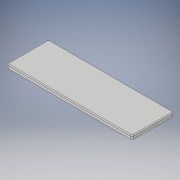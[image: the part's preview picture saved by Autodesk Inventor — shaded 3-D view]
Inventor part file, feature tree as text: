
AUTODESK INVENTOR PART (.ipt)
format: ipt  version: 2017 (Build 210142000, 142)  size: 111,616 bytes
history: native  units: in
note: dims shown in document units (in); Inventor stores cm internally (conversion verified against a paired STEP export)
features: extrude x1, fillet x1, sketch x1
ambient origin geometry x8: Origin, YZ Plane, XZ Plane, XY Plane, X Axis, Y Axis, Z Axis, Center Point
bodies: Solid1 (feature_tree)
feature tree (3):
  extrude  "main key board"  Depth=0.4792in
  fillet  "curved edges"  Radius=1.4583in
  sketch  "Sketch1"  dims[d4=0.0417in d5=0.4792in d6=1.4583in d7=0.0417in d8=0.0in d9=0.01in]
